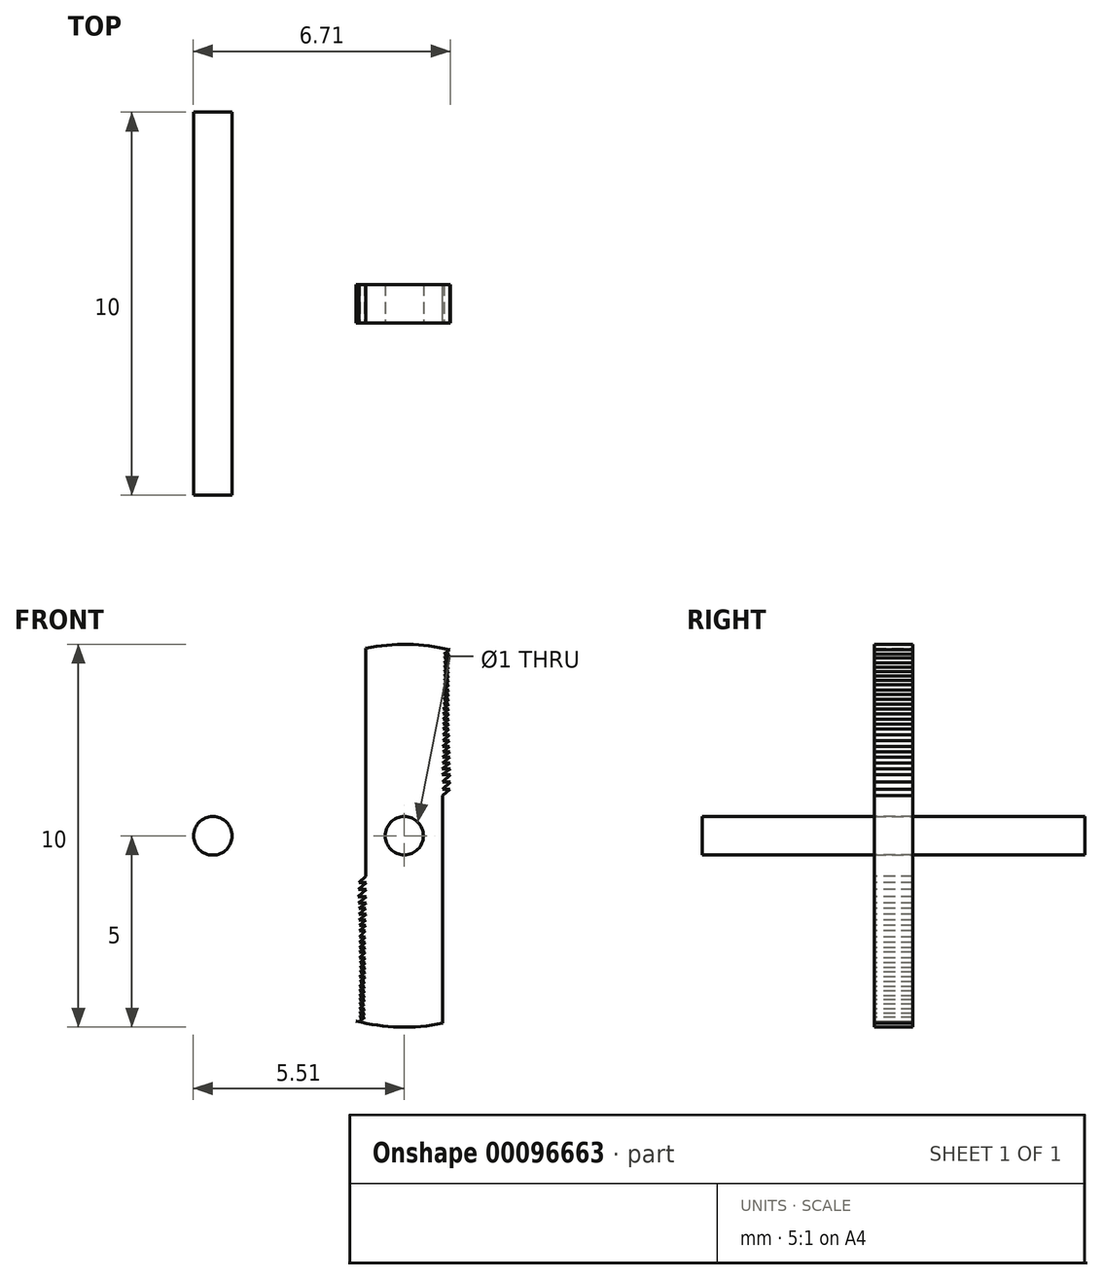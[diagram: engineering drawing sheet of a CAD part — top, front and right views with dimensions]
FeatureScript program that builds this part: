
annotation { "Feature Type Name" : "Feature", "Feature Type Description" : "" }
export const myFeature = defineFeature(function(context is Context, id is Id, definition is map)
    precondition{}
    {
        {
            var Q0;
            Q0=qCreatedBy(makeId("Front.planeOp"),FACE);
            var sketch = newSketch(context, id + "F0", { "sketchPlane" : qUnion([Q0])});
            skCircle(sketch, "E0", {"center": v(0, 0) * mm, "radius": 5 * mm});
            skSolve(sketch);
        }
        {
            var Q0;
            Q0 = qSketchRegion(id + "F0", true);
            extrude(context, id + "F1", {"entities" : qUnion([Q0]), "endBound" : BoundingType.SYMMETRIC, "depth" : 1 * mm});
        }
        {
            var Q0;
            Q0=qCreatedBy(makeId("Front.planeOp"),FACE);
            var sketch = newSketch(context, id + "F2", { "sketchPlane" : qUnion([Q0])});
            skLineSegment(sketch, "E1", {"start": v(0, 6.07) * mm, "end": v(0, -6) * mm});
            skCircle(sketch, "E2", {"center": v(0, 0) * mm, "radius": 1 * mm});
            skLineSegment(sketch, "E3", {"start": v(-1, 0) * mm, "end": v(-1, 4.92) * mm});
            skLineSegment(sketch, "E4", {"start": v(1, 0) * mm, "end": v(1, 1.05) * mm});
            skLineSegment(sketch, "E5", {"start": v(1, 1.05) * mm, "end": v(1.19, 1.22) * mm});
            skLineSegment(sketch, "E6", {"start": v(1.19, 1.22) * mm, "end": v(1, 1.22) * mm});
            skLineSegment(sketch, "E7", {"start": v(1, 1.22) * mm, "end": v(1.2, 1.4) * mm});
            skLineSegment(sketch, "E8", {"start": v(1.2, 1.4) * mm, "end": v(1, 1.4) * mm});
            skLineSegment(sketch, "E9", {"start": v(1, 1.4) * mm, "end": v(1.2, 1.6) * mm});
            skLineSegment(sketch, "E10", {"start": v(1.2, 1.6) * mm, "end": v(1, 1.6) * mm});
            skLineSegment(sketch, "E11", {"start": v(1, 1.6) * mm, "end": v(1.2, 1.75) * mm});
            skLineSegment(sketch, "E12", {"start": v(1.2, 1.75) * mm, "end": v(1, 1.75) * mm});
            skLineSegment(sketch, "E13", {"start": v(1, 1.75) * mm, "end": v(1.19, 1.9) * mm});
            skLineSegment(sketch, "E14", {"start": v(1.19, 1.9) * mm, "end": v(1, 1.9) * mm});
            skLineSegment(sketch, "E15", {"start": v(1, 1.9) * mm, "end": v(1.19, 2.05) * mm});
            skLineSegment(sketch, "E16", {"start": v(1.19, 2.05) * mm, "end": v(1, 2.05) * mm});
            skLineSegment(sketch, "E17", {"start": v(1, 2.05) * mm, "end": v(1.19, 2.2) * mm});
            skLineSegment(sketch, "E18", {"start": v(1.19, 2.2) * mm, "end": v(1, 2.2) * mm});
            skLineSegment(sketch, "E19", {"start": v(1, 2.2) * mm, "end": v(1.18, 2.34) * mm});
            skLineSegment(sketch, "E20", {"start": v(1.18, 2.34) * mm, "end": v(1, 2.34) * mm});
            skLineSegment(sketch, "E21", {"start": v(1, 2.34) * mm, "end": v(1.18, 2.49) * mm});
            skLineSegment(sketch, "E22", {"start": v(1.18, 2.49) * mm, "end": v(1.01, 2.49) * mm});
            skLineSegment(sketch, "E23", {"start": v(1.01, 2.49) * mm, "end": v(1.18, 2.64) * mm});
            skLineSegment(sketch, "E24", {"start": v(1.18, 2.64) * mm, "end": v(1.02, 2.64) * mm});
            skLineSegment(sketch, "E25", {"start": v(1.02, 2.64) * mm, "end": v(1.17, 2.79) * mm});
            skLineSegment(sketch, "E26", {"start": v(1.17, 2.79) * mm, "end": v(1.02, 2.79) * mm});
            skLineSegment(sketch, "E27", {"start": v(1.02, 2.79) * mm, "end": v(1.17, 2.92) * mm});
            skLineSegment(sketch, "E28", {"start": v(1.17, 2.92) * mm, "end": v(1.02, 2.92) * mm});
            skLineSegment(sketch, "E29", {"start": v(1.02, 2.92) * mm, "end": v(1.17, 3.05) * mm});
            skLineSegment(sketch, "E30", {"start": v(1.17, 3.05) * mm, "end": v(1.02, 3.05) * mm});
            skLineSegment(sketch, "E31", {"start": v(1.02, 3.05) * mm, "end": v(1.17, 3.19) * mm});
            skLineSegment(sketch, "E32", {"start": v(1.17, 3.19) * mm, "end": v(1.02, 3.19) * mm});
            skLineSegment(sketch, "E33", {"start": v(1.02, 3.19) * mm, "end": v(1.16, 3.32) * mm});
            skLineSegment(sketch, "E34", {"start": v(1.16, 3.32) * mm, "end": v(1.02, 3.32) * mm});
            skLineSegment(sketch, "E35", {"start": v(1.02, 3.32) * mm, "end": v(1.16, 3.44) * mm});
            skLineSegment(sketch, "E36", {"start": v(1.16, 3.44) * mm, "end": v(1.02, 3.44) * mm});
            skLineSegment(sketch, "E37", {"start": v(1.02, 3.44) * mm, "end": v(1.16, 3.56) * mm});
            skLineSegment(sketch, "E38", {"start": v(1.16, 3.56) * mm, "end": v(1.02, 3.56) * mm});
            skLineSegment(sketch, "E39", {"start": v(1.02, 3.56) * mm, "end": v(1.17, 3.69) * mm});
            skLineSegment(sketch, "E40", {"start": v(1.17, 3.69) * mm, "end": v(1.02, 3.69) * mm});
            skLineSegment(sketch, "E41", {"start": v(1.02, 3.69) * mm, "end": v(1.16, 3.81) * mm});
            skLineSegment(sketch, "E42", {"start": v(1.16, 3.81) * mm, "end": v(1.03, 3.81) * mm});
            skLineSegment(sketch, "E43", {"start": v(1.03, 3.81) * mm, "end": v(1.17, 3.94) * mm});
            skLineSegment(sketch, "E44", {"start": v(1.17, 3.94) * mm, "end": v(1.03, 3.94) * mm});
            skLineSegment(sketch, "E45", {"start": v(1.03, 3.94) * mm, "end": v(1.17, 4.06) * mm});
            skLineSegment(sketch, "E46", {"start": v(1.17, 4.06) * mm, "end": v(1.04, 4.06) * mm});
            skLineSegment(sketch, "E47", {"start": v(1.04, 4.06) * mm, "end": v(1.17, 4.18) * mm});
            skLineSegment(sketch, "E48", {"start": v(1.17, 4.18) * mm, "end": v(1.03, 4.18) * mm});
            skLineSegment(sketch, "E49", {"start": v(1.03, 4.18) * mm, "end": v(1.17, 4.29) * mm});
            skLineSegment(sketch, "E50", {"start": v(1.17, 4.29) * mm, "end": v(1.04, 4.29) * mm});
            skLineSegment(sketch, "E51", {"start": v(1.04, 4.29) * mm, "end": v(1.17, 4.4) * mm});
            skLineSegment(sketch, "E52", {"start": v(1.17, 4.4) * mm, "end": v(1.04, 4.4) * mm});
            skLineSegment(sketch, "E53", {"start": v(1.04, 4.4) * mm, "end": v(1.17, 4.52) * mm});
            skLineSegment(sketch, "E54", {"start": v(1.17, 4.52) * mm, "end": v(1.04, 4.52) * mm});
            skLineSegment(sketch, "E55", {"start": v(1.04, 4.52) * mm, "end": v(1.17, 4.64) * mm});
            skLineSegment(sketch, "E56", {"start": v(1.17, 4.64) * mm, "end": v(1.04, 4.64) * mm});
            skLineSegment(sketch, "E57", {"start": v(1.04, 4.64) * mm, "end": v(1.17, 4.75) * mm});
            skLineSegment(sketch, "E58", {"start": v(1.17, 4.75) * mm, "end": v(1.04, 4.75) * mm});
            skLineSegment(sketch, "E59", {"start": v(1.04, 4.75) * mm, "end": v(1.18, 4.85) * mm});
            skLineSegment(sketch, "E60.MirrorCS", {"start": v(-1.04, -4.75) * mm, "end": v(-1.18, -4.85) * mm});
            skLineSegment(sketch, "E61.MirrorCS", {"start": v(-1.17, -4.75) * mm, "end": v(-1.04, -4.75) * mm});
            skLineSegment(sketch, "E62.MirrorCS", {"start": v(-1.04, -4.64) * mm, "end": v(-1.17, -4.75) * mm});
            skLineSegment(sketch, "E63.MirrorCS", {"start": v(-1.17, -4.64) * mm, "end": v(-1.04, -4.64) * mm});
            skLineSegment(sketch, "E64.MirrorCS", {"start": v(-1.04, -4.52) * mm, "end": v(-1.17, -4.64) * mm});
            skLineSegment(sketch, "E65.MirrorCS", {"start": v(-1.17, -4.52) * mm, "end": v(-1.04, -4.52) * mm});
            skLineSegment(sketch, "E66.MirrorCS", {"start": v(-1.04, -4.4) * mm, "end": v(-1.17, -4.52) * mm});
            skLineSegment(sketch, "E67.MirrorCS", {"start": v(-1.17, -4.4) * mm, "end": v(-1.04, -4.4) * mm});
            skLineSegment(sketch, "E68.MirrorCS", {"start": v(-1.04, -4.29) * mm, "end": v(-1.17, -4.4) * mm});
            skLineSegment(sketch, "E69.MirrorCS", {"start": v(-1.17, -4.29) * mm, "end": v(-1.04, -4.29) * mm});
            skLineSegment(sketch, "E70.MirrorCS", {"start": v(-1.03, -4.18) * mm, "end": v(-1.17, -4.29) * mm});
            skLineSegment(sketch, "E71.MirrorCS", {"start": v(-1.17, -4.18) * mm, "end": v(-1.03, -4.18) * mm});
            skLineSegment(sketch, "E72.MirrorCS", {"start": v(-1.04, -4.06) * mm, "end": v(-1.17, -4.18) * mm});
            skLineSegment(sketch, "E73.MirrorCS", {"start": v(-1.17, -4.06) * mm, "end": v(-1.04, -4.06) * mm});
            skLineSegment(sketch, "E74.MirrorCS", {"start": v(-1.03, -3.94) * mm, "end": v(-1.17, -4.06) * mm});
            skLineSegment(sketch, "E75.MirrorCS", {"start": v(-1.17, -3.94) * mm, "end": v(-1.03, -3.94) * mm});
            skLineSegment(sketch, "E76.MirrorCS", {"start": v(-1.03, -3.81) * mm, "end": v(-1.17, -3.94) * mm});
            skLineSegment(sketch, "E77.MirrorCS", {"start": v(-1.16, -3.81) * mm, "end": v(-1.03, -3.81) * mm});
            skLineSegment(sketch, "E78.MirrorCS", {"start": v(-1.02, -3.69) * mm, "end": v(-1.16, -3.81) * mm});
            skLineSegment(sketch, "E79.MirrorCS", {"start": v(-1.17, -3.69) * mm, "end": v(-1.02, -3.69) * mm});
            skLineSegment(sketch, "E80.MirrorCS", {"start": v(-1.02, -3.56) * mm, "end": v(-1.17, -3.69) * mm});
            skLineSegment(sketch, "E81.MirrorCS", {"start": v(-1.16, -3.56) * mm, "end": v(-1.02, -3.56) * mm});
            skLineSegment(sketch, "E82.MirrorCS", {"start": v(-1.02, -3.44) * mm, "end": v(-1.16, -3.56) * mm});
            skLineSegment(sketch, "E83.MirrorCS", {"start": v(-1.16, -3.44) * mm, "end": v(-1.02, -3.44) * mm});
            skLineSegment(sketch, "E84.MirrorCS", {"start": v(-1.02, -3.32) * mm, "end": v(-1.16, -3.44) * mm});
            skLineSegment(sketch, "E85.MirrorCS", {"start": v(-1.16, -3.32) * mm, "end": v(-1.02, -3.32) * mm});
            skLineSegment(sketch, "E86.MirrorCS", {"start": v(-1.02, -3.19) * mm, "end": v(-1.16, -3.32) * mm});
            skLineSegment(sketch, "E87.MirrorCS", {"start": v(-1.17, -3.19) * mm, "end": v(-1.02, -3.19) * mm});
            skLineSegment(sketch, "E88.MirrorCS", {"start": v(-1.02, -3.05) * mm, "end": v(-1.17, -3.19) * mm});
            skLineSegment(sketch, "E89.MirrorCS", {"start": v(-1.17, -3.05) * mm, "end": v(-1.02, -3.05) * mm});
            skLineSegment(sketch, "E90.MirrorCS", {"start": v(-1, -1.05) * mm, "end": v(-1.2, -1.23) * mm});
            skLineSegment(sketch, "E91.MirrorCS", {"start": v(-1.19, -1.22) * mm, "end": v(-1, -1.22) * mm});
            skLineSegment(sketch, "E92.MirrorCS", {"start": v(-1, -1.22) * mm, "end": v(-1.2, -1.4) * mm});
            skLineSegment(sketch, "E93.MirrorCS", {"start": v(-1.2, -1.4) * mm, "end": v(-1, -1.4) * mm});
            skLineSegment(sketch, "E94.MirrorCS", {"start": v(-1, -1.4) * mm, "end": v(-1.2, -1.6) * mm});
            skLineSegment(sketch, "E95.MirrorCS", {"start": v(-1.2, -1.6) * mm, "end": v(-1, -1.6) * mm});
            skLineSegment(sketch, "E96.MirrorCS", {"start": v(-1, -1.6) * mm, "end": v(-1.2, -1.75) * mm});
            skLineSegment(sketch, "E97.MirrorCS", {"start": v(-1.2, -1.75) * mm, "end": v(-1, -1.75) * mm});
            skLineSegment(sketch, "E98.MirrorCS", {"start": v(-1, -1.75) * mm, "end": v(-1.19, -1.9) * mm});
            skLineSegment(sketch, "E99.MirrorCS", {"start": v(-1, -1.9) * mm, "end": v(-1.19, -2.05) * mm});
            skLineSegment(sketch, "E100.MirrorCS", {"start": v(-1.19, -1.9) * mm, "end": v(-1, -1.9) * mm});
            skLineSegment(sketch, "E101.MirrorCS", {"start": v(-1.19, -2.05) * mm, "end": v(-1, -2.05) * mm});
            skLineSegment(sketch, "E102.MirrorCS", {"start": v(-1, -2.05) * mm, "end": v(-1.19, -2.2) * mm});
            skLineSegment(sketch, "E103.MirrorCS", {"start": v(-1.19, -2.2) * mm, "end": v(-1, -2.2) * mm});
            skLineSegment(sketch, "E104.MirrorCS", {"start": v(-1, -2.2) * mm, "end": v(-1.18, -2.34) * mm});
            skLineSegment(sketch, "E105.MirrorCS", {"start": v(-1.18, -2.34) * mm, "end": v(-1, -2.34) * mm});
            skLineSegment(sketch, "E106.MirrorCS", {"start": v(-1, -2.34) * mm, "end": v(-1.18, -2.49) * mm});
            skLineSegment(sketch, "E107.MirrorCS", {"start": v(-1.18, -2.49) * mm, "end": v(-1.01, -2.49) * mm});
            skLineSegment(sketch, "E108.MirrorCS", {"start": v(-1.01, -2.49) * mm, "end": v(-1.18, -2.64) * mm});
            skLineSegment(sketch, "E109.MirrorCS", {"start": v(-1.18, -2.64) * mm, "end": v(-1.02, -2.64) * mm});
            skLineSegment(sketch, "E110.MirrorCS", {"start": v(-1.02, -2.64) * mm, "end": v(-1.17, -2.79) * mm});
            skLineSegment(sketch, "E111.MirrorCS", {"start": v(-1.17, -2.79) * mm, "end": v(-1.02, -2.79) * mm});
            skLineSegment(sketch, "E112.MirrorCS", {"start": v(-1.02, -2.79) * mm, "end": v(-1.17, -2.92) * mm});
            skLineSegment(sketch, "E113.MirrorCS", {"start": v(-1.17, -2.92) * mm, "end": v(-1.02, -2.92) * mm});
            skLineSegment(sketch, "E114.MirrorCS", {"start": v(-1.02, -2.92) * mm, "end": v(-1.17, -3.05) * mm});
            skLineSegment(sketch, "E115.MirrorCS", {"start": v(-1, 0) * mm, "end": v(-1, -1.05) * mm});
            skLineSegment(sketch, "E116", {"start": v(1, 0) * mm, "end": v(1, -4.97) * mm});
            skLineSegment(sketch, "E117", {"start": v(1, -4.97) * mm, "end": v(3.53, -4.42) * mm});
            skLineSegment(sketch, "E118", {"start": v(3.53, -4.42) * mm, "end": v(5.06, -2.45) * mm});
            skLineSegment(sketch, "E119", {"start": v(5.06, -2.45) * mm, "end": v(5.48, 0.58) * mm});
            skLineSegment(sketch, "E120", {"start": v(5.48, 0.58) * mm, "end": v(4.62, 3.3) * mm});
            skLineSegment(sketch, "E121", {"start": v(4.62, 3.3) * mm, "end": v(1.76, 4.94) * mm});
            skLineSegment(sketch, "E122", {"start": v(1.76, 4.94) * mm, "end": v(1.18, 4.85) * mm});
            skLineSegment(sketch, "E123", {"start": v(-1.18, -4.85) * mm, "end": v(-3.13, -4.46) * mm});
            skLineSegment(sketch, "E124", {"start": v(-3.13, -4.46) * mm, "end": v(-5.1, -1.93) * mm});
            skLineSegment(sketch, "E125", {"start": v(-5.1, -1.93) * mm, "end": v(-5.55, 1.31) * mm});
            skLineSegment(sketch, "E126", {"start": v(-5.55, 1.31) * mm, "end": v(-4.2, 3.55) * mm});
            skLineSegment(sketch, "E127", {"start": v(-4.2, 3.55) * mm, "end": v(-1.64, 5.04) * mm});
            skLineSegment(sketch, "E128", {"start": v(-1.64, 5.04) * mm, "end": v(-1, 4.92) * mm});
            skSolve(sketch);
        }
        {
            var Q0;
            Q0=makeQuery(id+"F2.imprint","IMPRINT",FACE,{"disambiguationData":[TD([[makeQuery(id+"F2.imprint","IMPRINT",EDGE,{"derivedFrom":sQuery(id+"F2.wireOp",EDGE,"E3")}),1.0]])]});
            var Q1;
            Q1=makeQuery(id+"F2.imprint","IMPRINT",FACE,{"disambiguationData":[TD([[makeQuery(id+"F2.imprint","IMPRINT",EDGE,{"derivedFrom":sQuery(id+"F2.wireOp",EDGE,"E4")}),-1.0]])]});
            extrude(context, id + "F3", {"entities" : qUnion([Q0, Q1]), "operationType" : NewBodyOperationType.REMOVE, "endBound" : BoundingType.SYMMETRIC, "oppositeDirection" : true, "depth" : 25 * mm});
        }
        {
            var Q0;
            Q0=sQuery(id+"F2.wireOp",VERTEX,"E2.center");
            var Q1;
            Q1=makeQuery(id+"F1.opExtrude","SWEPT_BODY",BODY,{"disambiguationData":[OSD([sQuery(id+"F0.wireOp",EDGE,"E0")])]});
            hole(context, id + "F4", {"style" : HoleStyle.SIMPLE, "endStyle" : HoleEndStyle.BLIND, "holeDiameter" : 1 * mm, "holeDepth" : 25 * mm, "locations" : qUnion([Q0]), "scope" : qUnion([Q1])});
        }
        {
            var Q0;
            Q0=sQuery(id+"F2.wireOp",VERTEX,"E2.center");
            var Q1;
            Q1=makeQuery(id+"F1.opExtrude","SWEPT_BODY",BODY,{"disambiguationData":[OSD([sQuery(id+"F0.wireOp",EDGE,"E0")])]});
            hole(context, id + "F5", {"style" : HoleStyle.SIMPLE, "endStyle" : HoleEndStyle.BLIND, "oppositeDirection" : true, "holeDiameter" : 1 * mm, "holeDepth" : 25 * mm, "locations" : qUnion([Q0]), "scope" : qUnion([Q1])});
        }
        {
            var Q0;
            Q0=makeQuery(id+"F1.opExtrude","SWEPT_BODY",BODY,{"disambiguationData":[OSD([sQuery(id+"F0.wireOp",EDGE,"E0")])]});
            transform(context, id + "F6", {"entities" : qUnion([Q0]), "transformType" : TransformType.TRANSLATION_3D, "dx" : 60 * mm, "dy" : 0 * mm, "dz" : 0 * mm, "makeCopy" : false});
        }
        {
            var Q0;
            Q0=qCreatedBy(makeId("Front.planeOp"),FACE);
            var sketch = newSketch(context, id + "F7", { "sketchPlane" : qUnion([Q0])});
            skCircle(sketch, "E129", {"center": v(0, 0) * mm, "radius": 0.5 * mm});
            skSolve(sketch);
        }
        {
            var Q0;
            Q0=makeQuery(id+"F7.imprint","IMPRINT",FACE,{"disambiguationData":[TD([[makeQuery(id+"F7.imprint","IMPRINT",EDGE,{"derivedFrom":sQuery(id+"F7.wireOp",EDGE,"E129")}),1.0]])]});
            extrude(context, id + "F8", {"entities" : qUnion([Q0]), "endBound" : BoundingType.SYMMETRIC, "depth" : 10 * mm});
        }
        {
            var Q0;
            Q0=makeQuery(id+"F8.opExtrude","SWEPT_BODY",BODY,{"disambiguationData":[OSD([sQuery(id+"F7.wireOp",EDGE,"E129")])]});
            transform(context, id + "F9", {"entities" : qUnion([Q0]), "transformType" : TransformType.TRANSLATION_3D, "dx" : 55 * mm, "dy" : 0 * mm, "dz" : 0 * mm, "makeCopy" : false});
        }
    });
